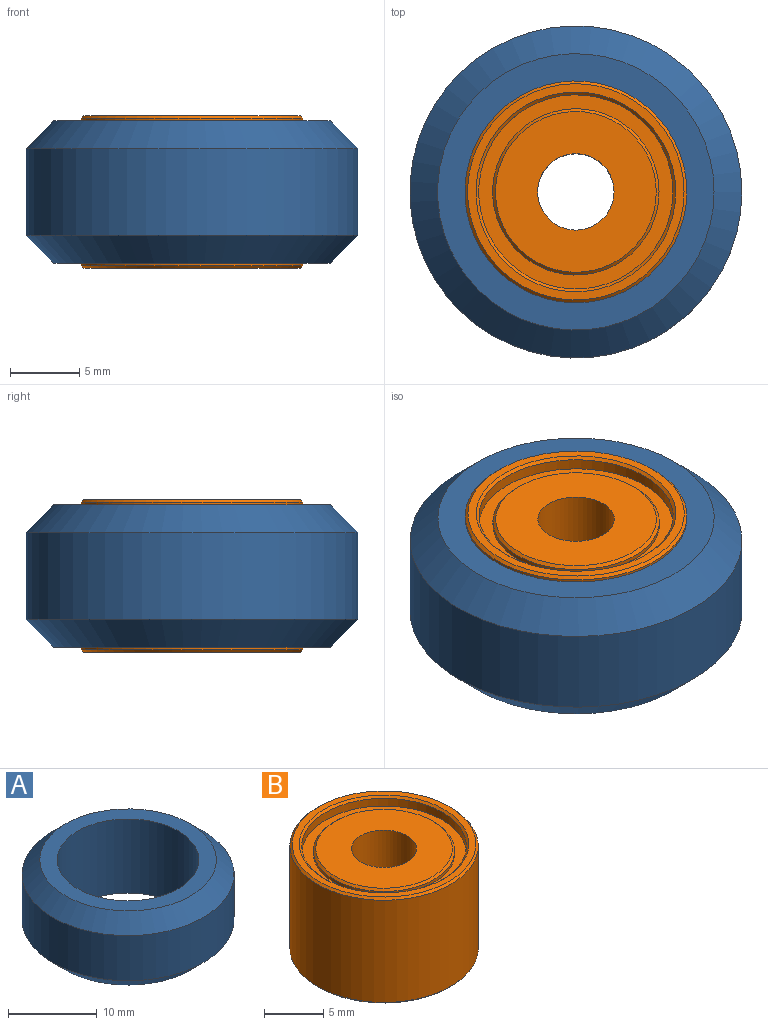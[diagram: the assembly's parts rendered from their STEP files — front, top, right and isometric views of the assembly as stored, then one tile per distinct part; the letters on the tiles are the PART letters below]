
ASSEMBLY  parts=2 mates=1
PART A: 6 faces, bbox 23.9x23.9x10.2 mm
  f0: cylinder r=7.99mm len=15.97mm, axis (0,0,-1), area 513.3mm2, adj f2,f3
  f1: cylinder r=11.95mm len=23.89mm, axis (0,0,-1), area 467.6mm2, adj f4,f5
  f2: plane 19.89x19.89mm, normal (0,0,1), area 110.4mm2, adj f0,f5
  f3: plane 19.89x19.89mm, normal (0,0,-1), area 110.4mm2, adj f0,f4
  f4: cone r=11.95mm half-angle=45deg, axis (0,0,1), area 194.5mm2, adj f1,f3
  f5: cone r=9.95mm half-angle=45deg, axis (0,0,-1), area 194.5mm2, adj f1,f2
PART B: 18 faces, bbox 16x16x11 mm
  f0: cylinder r=6.99mm len=13.97mm, axis (0,0,-1), area 35.1mm2, adj f6,f13
  f1: cylinder r=6.99mm len=13.97mm, axis (0,0,-1), area 35.1mm2, adj f5,f16
  f2: cylinder r=7.99mm len=15.97mm, axis (0,0,-1), area 531.8mm2, adj f14,f17
  f3: plane 15.57x15.57mm, normal (0,0,1), area 28.2mm2, adj f16,f17
  f4: plane 15.57x15.57mm, normal (0,0,-1), area 28.2mm2, adj f13,f14
  f5: plane 13.97x13.97mm, normal (0,0,1), area 40.7mm2, adj f1,f9
  f6: plane 13.97x13.97mm, normal (0,0,-1), area 40.7mm2, adj f0,f8
  f7: plane 11.57x11.57mm, normal (0,0,-1), area 81.4mm2, adj f11,f12
  f8: cylinder r=5.98mm len=11.97mm, axis (0,0,-1), area 11.3mm2, adj f6,f12
  f9: cylinder r=5.98mm len=11.97mm, axis (0,0,-1), area 11.3mm2, adj f5,f15
  f10: plane 11.57x11.57mm, normal (0,0,1), area 81.4mm2, adj f11,f15
  f11: cylinder r=2.75mm len=10mm, axis (0,0,1), area 172.8mm2, adj f7,f10
  f12: cone r=5.98mm half-angle=45deg, axis (0,0,1), area 10.5mm2, adj f7,f8
  f13: cone r=7.19mm half-angle=45deg, axis (0,0,-1), area 12.6mm2, adj f0,f4
  f14: cone r=7.99mm half-angle=45deg, axis (0,0,1), area 14mm2, adj f2,f4
  f15: cone r=5.79mm half-angle=45deg, axis (0,0,-1), area 10.5mm2, adj f9,f10
  f16: cone r=6.99mm half-angle=45deg, axis (0,0,1), area 12.6mm2, adj f1,f3
  f17: cone r=7.79mm half-angle=45deg, axis (0,0,-1), area 14mm2, adj f2,f3
PLACE A at identity
PLACE B at identity fixed
MATE fastened A.f1 <-> B.f11  axis (0,0,-1) through (0,0,0)mm
